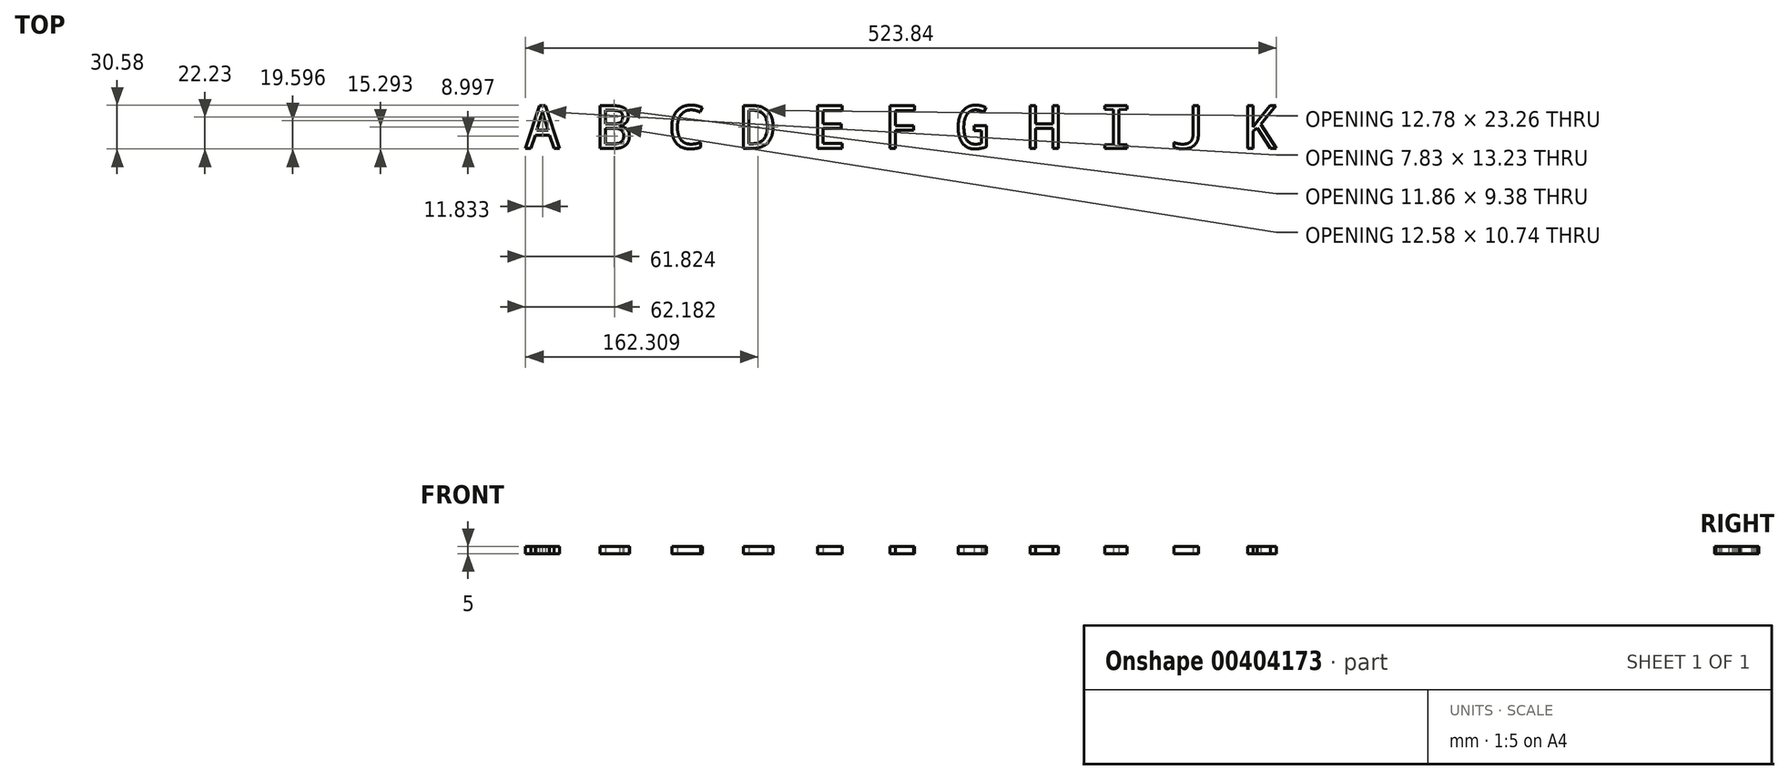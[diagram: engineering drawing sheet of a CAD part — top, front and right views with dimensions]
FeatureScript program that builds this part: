
annotation { "Feature Type Name" : "Feature", "Feature Type Description" : "" }
export const myFeature = defineFeature(function(context is Context, id is Id, definition is map)
    precondition{}
    {
        {
            var Q0;
            Q0=qCreatedBy(makeId("Top.planeOp"),FACE);
            var sketch = newSketch(context, id + "F0", { "sketchPlane" : qUnion([Q0])});
            skText(sketch, "E0", { "text": "A B C D E F G H I J K", "fontName": "DroidSansMono.ttf"});
            const initialGuessF0  = {"E0": [-0.0262, -0.01534, 1, 0, 0.03]};
            skSetInitialGuess(sketch, initialGuessF0);
            skSolve(sketch);
        }
        {
            var Q0;
            Q0 = qSketchRegion(id + "F0", true);
            extrude(context, id + "F1", {"entities" : qUnion([Q0]), "depth" : 5 * mm});
        }
    });
